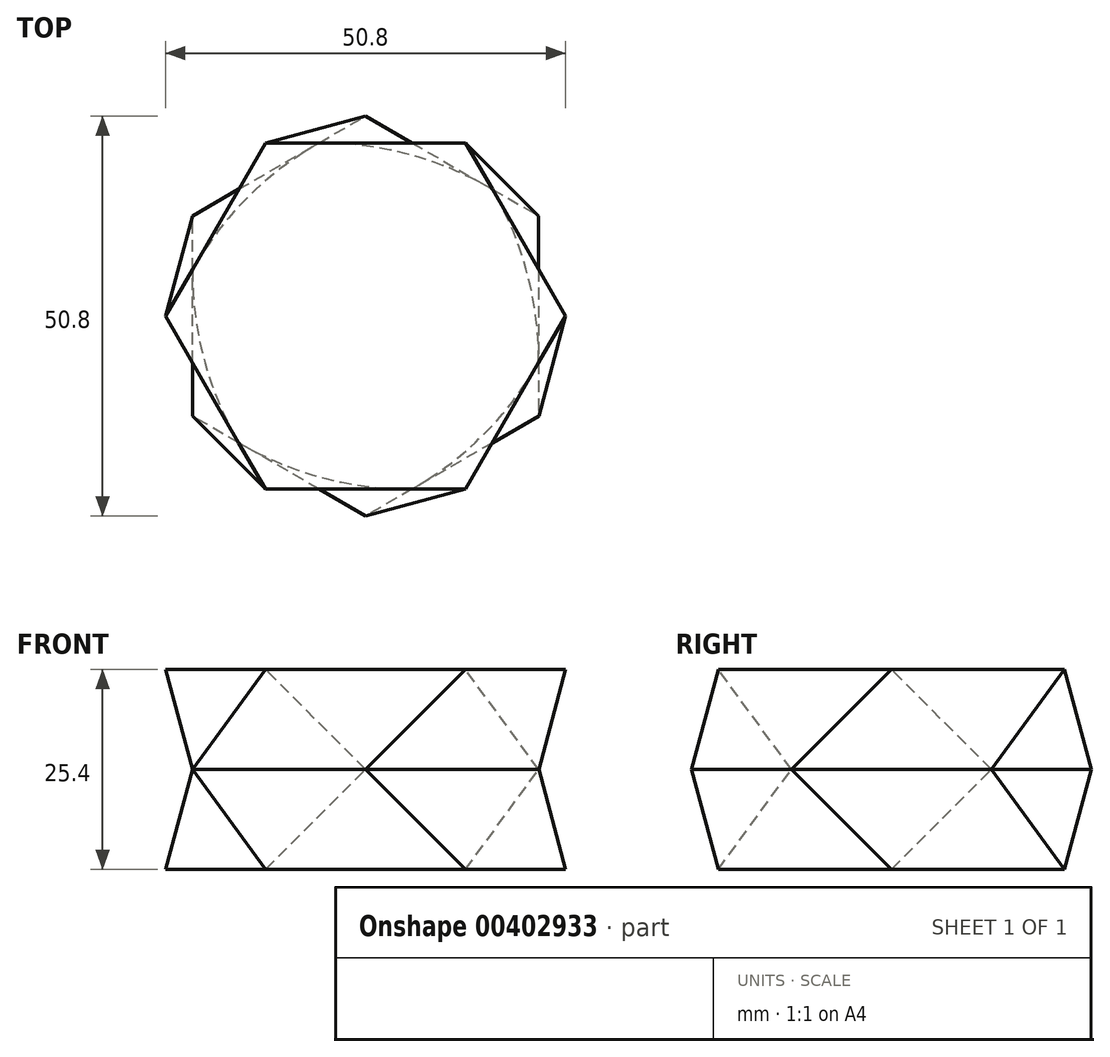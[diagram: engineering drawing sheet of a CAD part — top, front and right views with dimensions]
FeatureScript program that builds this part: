
annotation { "Feature Type Name" : "Feature", "Feature Type Description" : "" }
export const myFeature = defineFeature(function(context is Context, id is Id, definition is map)
    precondition{}
    {
        {
            var Q0;
            Q0=qCreatedBy(makeId("Top.planeOp"),FACE);
            var sketch = newSketch(context, id + "F0", { "sketchPlane" : qUnion([Q0])});
            skCircle(sketch, "E0.cCircle", {"center": v(0, 0) * mm, "radius": 22 * mm, "construction": true});
            skLineSegment(sketch, "E0.0", {"start": v(-12.7, 22) * mm, "end": v(12.7, 22) * mm});
            skLineSegment(sketch, "E0.1", {"start": v(12.7, 22) * mm, "end": v(25.4, 0) * mm});
            skLineSegment(sketch, "E0.2", {"start": v(25.4, 0) * mm, "end": v(12.7, -22) * mm});
            skLineSegment(sketch, "E0.3", {"start": v(12.7, -22) * mm, "end": v(-12.7, -22) * mm});
            skLineSegment(sketch, "E0.4", {"start": v(-12.7, -22) * mm, "end": v(-25.4, 0) * mm});
            skLineSegment(sketch, "E0.5", {"start": v(-25.4, 0) * mm, "end": v(-12.7, 22) * mm});
            skPoint(sketch, "E0.0.midPoint", {"position": v(0, 22) * mm});
            skSolve(sketch);
        }
        {
            var Q0;
            Q0=qCreatedBy(makeId("Top.planeOp"),FACE);
            cPlane(context, id + "F1", {"entities" : qUnion([Q0]), "cplaneType" : CPlaneType.OFFSET, "offset" : 12.7 * mm, "width" : 152.4 * mm, "height" : 152.4 * mm});
        }
        {
            var Q0;
            Q0=qCreatedBy(id+"F1.planeOp",FACE);
            var sketch = newSketch(context, id + "F2", { "sketchPlane" : qUnion([Q0])});
            skCircle(sketch, "E1.cCircle", {"center": v(0, 0) * mm, "radius": 22 * mm, "construction": true});
            skLineSegment(sketch, "E1.0", {"start": v(-22, 12.7) * mm, "end": v(0, 25.4) * mm});
            skLineSegment(sketch, "E1.1", {"start": v(0, 25.4) * mm, "end": v(22, 12.7) * mm});
            skLineSegment(sketch, "E1.2", {"start": v(22, 12.7) * mm, "end": v(22, -12.7) * mm});
            skLineSegment(sketch, "E1.3", {"start": v(22, -12.7) * mm, "end": v(0, -25.4) * mm});
            skLineSegment(sketch, "E1.4", {"start": v(0, -25.4) * mm, "end": v(-22, -12.7) * mm});
            skLineSegment(sketch, "E1.5", {"start": v(-22, -12.7) * mm, "end": v(-22, 12.7) * mm});
            skPoint(sketch, "E1.0.midPoint", {"position": v(-11, 19.05) * mm});
            skSolve(sketch);
        }
        {
            var Q0;
            Q0=makeQuery(id+"F0.imprint","IMPRINT",FACE,{"disambiguationData":[TD([[makeQuery(id+"F0.imprint","IMPRINT",EDGE,{"derivedFrom":sQuery(id+"F0.wireOp",EDGE,"E0.0")}),-1.0]])]});
            var Q1;
            Q1=makeQuery(id+"F2.imprint","IMPRINT",FACE,{"disambiguationData":[TD([[makeQuery(id+"F2.imprint","IMPRINT",EDGE,{"derivedFrom":sQuery(id+"F2.wireOp",EDGE,"E1.0")}),-1.0]])]});
            loft(context, id + "F3", {"sheetProfilesArray" : [{ "sheetProfileEntities" : qUnion([Q0]) }, { "sheetProfileEntities" : qUnion([Q1]) }]});
        }
        {
            var Q0;
            Q0=qCreatedBy(id+"F1.planeOp",FACE);
            cPlane(context, id + "F4", {"entities" : qUnion([Q0]), "cplaneType" : CPlaneType.OFFSET, "offset" : 12.7 * mm, "width" : 152.4 * mm, "height" : 152.4 * mm});
        }
        {
            var Q0;
            Q0=qCreatedBy(id+"F4.planeOp",FACE);
            var sketch = newSketch(context, id + "F5", { "sketchPlane" : qUnion([Q0])});
            skCircle(sketch, "E2.cCircle", {"center": v(0, 0) * mm, "radius": 22 * mm, "construction": true});
            skLineSegment(sketch, "E2.0", {"start": v(-12.7, 22) * mm, "end": v(12.7, 22) * mm});
            skLineSegment(sketch, "E2.1", {"start": v(12.7, 22) * mm, "end": v(25.4, 0) * mm});
            skLineSegment(sketch, "E2.2", {"start": v(25.4, 0) * mm, "end": v(12.7, -22) * mm});
            skLineSegment(sketch, "E2.3", {"start": v(12.7, -22) * mm, "end": v(-12.7, -22) * mm});
            skLineSegment(sketch, "E2.4", {"start": v(-12.7, -22) * mm, "end": v(-25.4, 0) * mm});
            skLineSegment(sketch, "E2.5", {"start": v(-25.4, 0) * mm, "end": v(-12.7, 22) * mm});
            skPoint(sketch, "E2.0.midPoint", {"position": v(0, 22) * mm});
            skSolve(sketch);
        }
        {
            var Q1;
            Q1=makeQuery(id+"F3.opLoft","CAP_FACE",FACE,{"disambiguationData":[OSD([makeQuery(id+"F2.imprint","IMPRINT",FACE,{"disambiguationData":[TD([[makeQuery(id+"F2.imprint","IMPRINT",EDGE,{"derivedFrom":sQuery(id+"F2.wireOp",EDGE,"E1.0")}),-1.0]])]})])],"isStart":true});
            var Q2;
            Q2=makeQuery(id+"F5.imprint","IMPRINT",FACE,{"disambiguationData":[TD([[makeQuery(id+"F5.imprint","IMPRINT",EDGE,{"derivedFrom":sQuery(id+"F5.wireOp",EDGE,"E2.0")}),-1.0]])]});
            loft(context, id + "F6", {"operationType" : NewBodyOperationType.ADD, "sheetProfilesArray" : [{ "sheetProfileEntities" : qUnion([Q1]) }, { "sheetProfileEntities" : qUnion([Q2]) }]});
        }
    });
